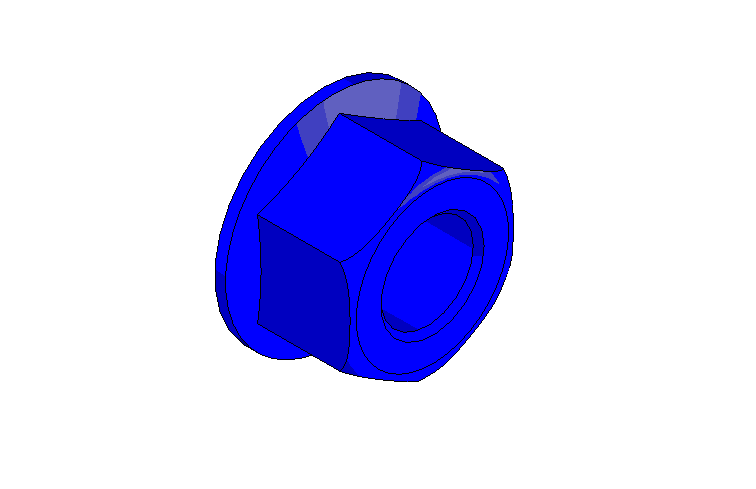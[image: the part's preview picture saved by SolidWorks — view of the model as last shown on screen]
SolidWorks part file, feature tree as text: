
SOLIDWORKS PART (.sldprt)
format: sldprt  version: not decoded by parser v0  size: 228,352 bytes
history: native  units: mm
features: sketch x4, plane x3, material x1, extrude x1, cut_revolve x1, revolve x1, cut_extrude x1, chamfer x1 (+10 scaffold rows collapsed)
feature tree (23):
  scaffold x10  (default folders/planes/origin — collapsed)
  material  "Matériau <non spécifié>"
  plane  "Plan de face"
  plane  "Plan de dessus"
  plane  "Plan de droite"
  sketch  "Esquisse1"  dims[D1=15.0mm]
  extrude  "Extrusion1"  Depth=10mm
  sketch  "Esquisse2"  dims[D1=14.0mm D2=1.0mm]
  cut_revolve  "Enlèvement de matière-Révolution1"  Angle=360deg
  sketch  "Esquisse3"  dims[D3=30.0mm D1=1.0mm D2=20.0mm]
  revolve  "Révolution1"  Angle=360deg
  sketch  "Esquisse4"  dims[D1=8.5mm]
  cut_extrude  "Enlèv. mat.-Extru.2"  Depth=10mm
  chamfer  "Chanfrein1"  Distance=0.5mm Angle=45deg
decode coverage: 9 of 9 modeling features carry decoded parameters
note: suppression state not decoded; provenance and decode notes live in map.json
